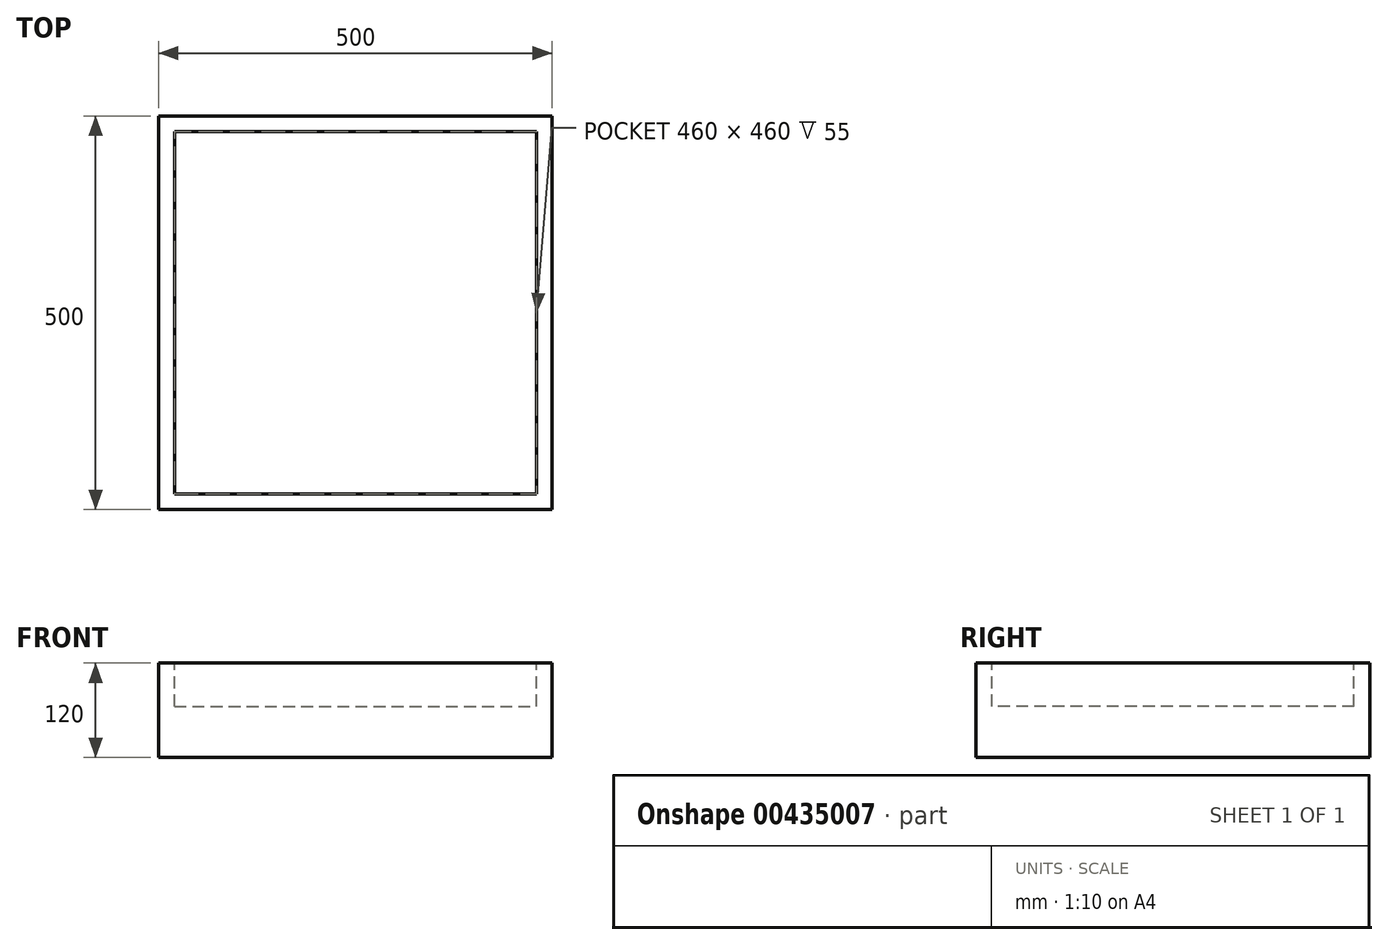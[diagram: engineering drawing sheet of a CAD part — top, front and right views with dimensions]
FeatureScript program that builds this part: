
annotation { "Feature Type Name" : "Feature", "Feature Type Description" : "" }
export const myFeature = defineFeature(function(context is Context, id is Id, definition is map)
    precondition{}
    {
        {
            var Q0;
            Q0=qCreatedBy(makeId("Front.planeOp"),FACE);
            var sketch = newSketch(context, id + "F0", { "sketchPlane" : qUnion([Q0])});
            skLineSegment(sketch, "E0.bottom", {"start": v(0, 0) * mm, "end": v(500, 0) * mm});
            skLineSegment(sketch, "E0.top", {"start": v(0, 120) * mm, "end": v(500, 120) * mm});
            skLineSegment(sketch, "E0.left", {"start": v(0, 0) * mm, "end": v(0, 120) * mm});
            skLineSegment(sketch, "E0.right", {"start": v(500, 0) * mm, "end": v(500, 120) * mm});
            skSolve(sketch);
        }
        {
            var Q0;
            Q0=makeQuery(id+"F0.imprint","IMPRINT",FACE,{"disambiguationData":[TD([[makeQuery(id+"F0.imprint","IMPRINT",EDGE,{"derivedFrom":sQuery(id+"F0.wireOp",EDGE,"E0.bottom")}),1.0]])]});
            extrude(context, id + "F1", {"entities" : qUnion([Q0]), "oppositeDirection" : true, "depth" : 500 * mm});
        }
        {
            var Q0;
            Q0=makeQuery(id+"F1.opExtrude","SWEPT_FACE",FACE,{"disambiguationData":[OSD([sQuery(id+"F0.wireOp",EDGE,"E0.top")])]});
            shell(context, id + "F2", {"entities" : qUnion([Q0]), "thickness" : 20 * mm});
        }
        {
            var Q0;
            Q0=makeQuery(id+"F2.opShell","OFFSET_FACE",FACE,{"disambiguationData":[OSD([sQuery(id+"F0.wireOp",EDGE,"E0.bottom")])]});
            var sketch = newSketch(context, id + "F3", { "sketchPlane" : qUnion([Q0])});
            skLineSegment(sketch, "E1.bottom", {"start": v(20, 480) * mm, "end": v(480, 480) * mm});
            skLineSegment(sketch, "E1.top", {"start": v(20, 20) * mm, "end": v(480, 20) * mm});
            skLineSegment(sketch, "E1.left", {"start": v(20, 480) * mm, "end": v(20, 20) * mm});
            skLineSegment(sketch, "E1.right", {"start": v(480, 480) * mm, "end": v(480, 20) * mm});
            skSolve(sketch);
        }
        {
            var Q0;
            Q0 = qSketchRegion(id + "F3", true);
            extrude(context, id + "F4", {"entities" : qUnion([Q0]), "operationType" : NewBodyOperationType.ADD, "depth" : 45 * mm});
        }
    });
